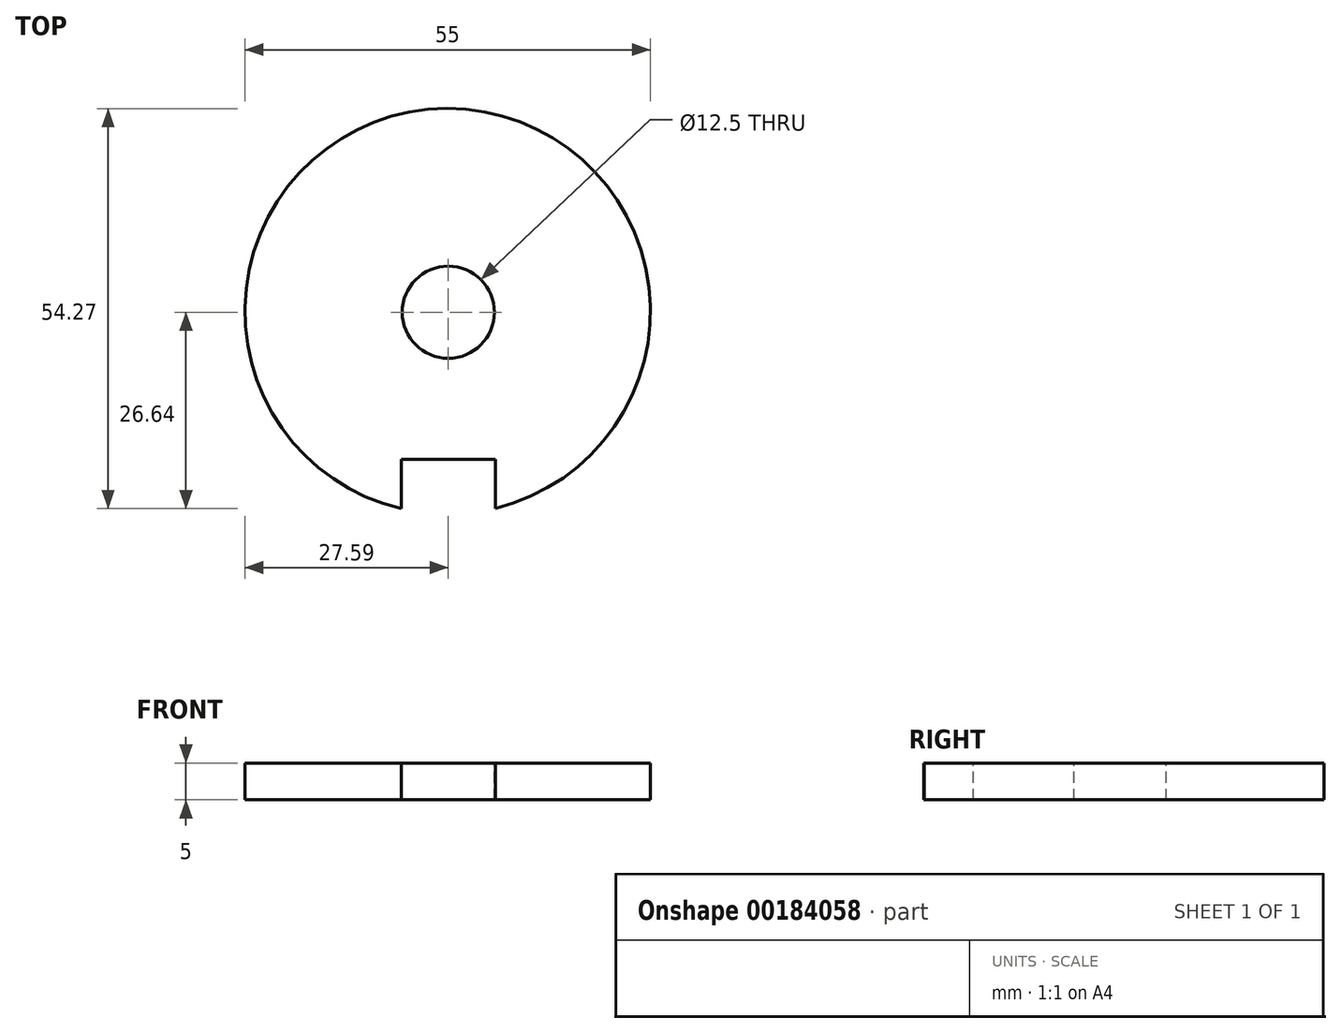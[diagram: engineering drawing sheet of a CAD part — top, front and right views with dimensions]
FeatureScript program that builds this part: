
annotation { "Feature Type Name" : "Feature", "Feature Type Description" : "" }
export const myFeature = defineFeature(function(context is Context, id is Id, definition is map)
    precondition{}
    {
        {
            var Q0;
            Q0=qCreatedBy(makeId("Top.planeOp"),FACE);
            var sketch = newSketch(context, id + "F0", { "sketchPlane" : qUnion([Q0])});
            skCircle(sketch, "E0", {"center": v(-0.1, 0.13) * mm, "radius": 27.5 * mm});
            skSolve(sketch);
        }
        {
            var Q0;
            Q0=makeQuery(id+"F0.imprint","IMPRINT",FACE,{"disambiguationData":[TD([[makeQuery(id+"F0.imprint","IMPRINT",EDGE,{"derivedFrom":sQuery(id+"F0.wireOp",EDGE,"E0")}),1.0]])]});
            extrude(context, id + "F1", {"entities" : qUnion([Q0]), "depth" : 5 * mm});
        }
        {
            var Q0;
            Q0=makeQuery(id+"F1.opExtrude","CAP_FACE",FACE,{"disambiguationData":[OSD([sQuery(id+"F0.wireOp",EDGE,"E0")])],"isStart":false});
            var sketch = newSketch(context, id + "F2", { "sketchPlane" : qUnion([Q0])});
            skCircle(sketch, "E1", {"center": v(0, 0) * mm, "radius": 6.25 * mm});
            skSolve(sketch);
        }
        {
            var Q0;
            Q0 = qSketchRegion(id + "F2", true);
            extrude(context, id + "F3", {"entities" : qUnion([Q0]), "operationType" : NewBodyOperationType.REMOVE, "oppositeDirection" : true, "depth" : 25 * mm});
        }
        {
            var Q0;
            Q0=makeQuery(id+"F1.opExtrude","CAP_FACE",FACE,{"disambiguationData":[OSD([sQuery(id+"F0.wireOp",EDGE,"E0")])],"isStart":false});
            var sketch = newSketch(context, id + "F4", { "sketchPlane" : qUnion([Q0])});
            skLineSegment(sketch, "E2.bottom", {"start": v(-4.24, -28.63) * mm, "end": v(5.4, -28.63) * mm});
            skLineSegment(sketch, "E2.top", {"start": v(-4.24, -20.92) * mm, "end": v(5.4, -20.92) * mm});
            skLineSegment(sketch, "E2.left", {"start": v(-4.24, -20.92) * mm, "end": v(-4.24, -28.63) * mm});
            skLineSegment(sketch, "E2.right", {"start": v(5.4, -20.92) * mm, "end": v(5.4, -28.63) * mm});
            skSolve(sketch);
        }
        {
            var Q0;
            {var subQ0=sQuery(id+"F4.wireOp",EDGE,"E2.top");Q0=makeQuery(id+"F4.imprint","IMPRINT",FACE,{"disambiguationData":[TD([[makeQuery(id+"F4.imprint","IMPRINT",EDGE,{"derivedFrom":subQ0}),-1.0]])]});}
            var Q1;
            Q1=sQuery(id+"F4.wireOp",EDGE,"E2.right");
            var Q2;
            Q2=sQuery(id+"F4.wireOp",EDGE,"E2.left");
            var Q3;
            Q3=sQuery(id+"F4.wireOp",EDGE,"E2.bottom");
            extrude(context, id + "F5", {"entities" : qUnion([Q0]), "operationType" : NewBodyOperationType.REMOVE, "surfaceEntities" : qUnion([Q1, Q2, Q3]), "oppositeDirection" : true, "depth" : 5 * mm});
        }
        {
            var Q0;
            Q0=makeQuery(id+"F1.opExtrude","CAP_FACE",FACE,{"disambiguationData":[OSD([sQuery(id+"F0.wireOp",EDGE,"E0")])],"isStart":false});
            var sketch = newSketch(context, id + "F6", { "sketchPlane" : qUnion([Q0])});
            skLineSegment(sketch, "E3.bottom", {"start": v(-6.36, -19.95) * mm, "end": v(6.36, -19.95) * mm});
            skLineSegment(sketch, "E3.top", {"start": v(-6.36, -29.78) * mm, "end": v(6.36, -29.78) * mm});
            skLineSegment(sketch, "E3.left", {"start": v(-6.36, -19.95) * mm, "end": v(-6.36, -29.78) * mm});
            skLineSegment(sketch, "E3.right", {"start": v(6.36, -19.95) * mm, "end": v(6.36, -29.78) * mm});
            skSolve(sketch);
        }
        {
            var Q0;
            {var subQ0=sQuery(id+"F6.wireOp",EDGE,"E3.bottom");Q0=makeQuery(id+"F6.imprint","IMPRINT",FACE,{"disambiguationData":[TD([[makeQuery(id+"F6.imprint","IMPRINT",EDGE,{"derivedFrom":subQ0}),-1.0]])]});}
            extrude(context, id + "F7", {"entities" : qUnion([Q0]), "operationType" : NewBodyOperationType.REMOVE, "oppositeDirection" : true, "depth" : 25 * mm});
        }
    });
